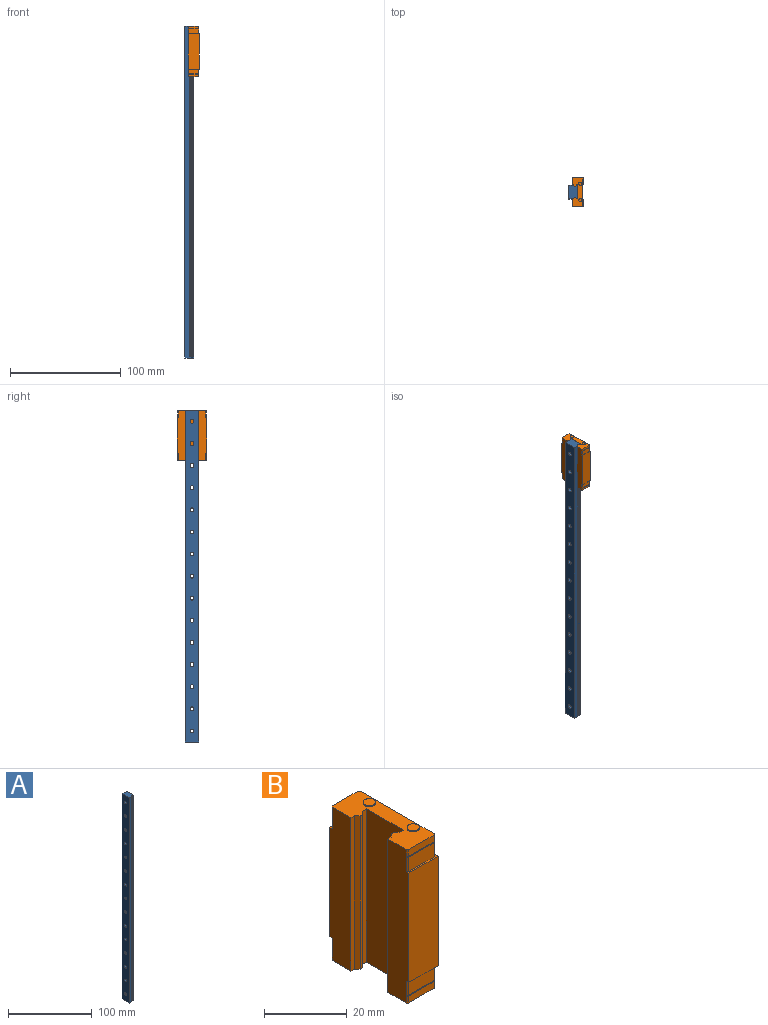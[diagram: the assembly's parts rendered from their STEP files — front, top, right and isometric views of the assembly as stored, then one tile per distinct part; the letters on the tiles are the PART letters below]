
ASSEMBLY  parts=2 mates=1
PART A: 59 faces, bbox 8x12x300 mm
  f0: plane 300x12mm, normal (1,0,0), area 3175.9mm2, adj f10,f11,f13,f15,f18,f21,f24,f27
  f1: cylinder r=1.75mm len=5.5mm, axis (-1,0,0), area 60.5mm2, adj f5,f14
  f2: plane 300x1mm, normal (0,1,0), area 300mm2, adj f3,f11,f12,f56
  f3: plane 300x1mm, normal (0.71,0.71,0), area 424.3mm2, adj f2,f4,f11,f56
  f4: plane 300x4mm, normal (0,1,0), area 1200mm2, adj f3,f5,f11,f56
  f5: plane 300x12mm, normal (-1,0,0), area 3455.7mm2, adj f1,f4,f6,f11,f16,f19,f22,f25
  f6: plane 300x4mm, normal (0,-1,0), area 1200mm2, adj f5,f7,f11,f56
  f7: plane 300x1mm, normal (0.71,-0.71,0), area 424.3mm2, adj f6,f8,f11,f56
  f8: plane 300x1mm, normal (0,-1,0), area 300mm2, adj f7,f9,f11,f56
  f9: plane 300x1mm, normal (-0.71,-0.71,0), area 424.3mm2, adj f8,f10,f11,f56
  f10: plane 300x1mm, normal (0,-1,0), area 300mm2, adj f0,f9,f11,f56
  f11: plane 12x8mm, normal (0,0,-1), area 92mm2, adj f0,f2,f3,f4,f5,f6,f7,f8
  f12: plane 300x1mm, normal (-0.71,0.71,0), area 424.3mm2, adj f2,f11,f13,f56
  f13: plane 300x1mm, normal (0,1,0), area 300mm2, adj f0,f11,f12,f56
  f14: plane 6x6mm, normal (1,0,0), area 18.7mm2, adj f1,f15
  f15: cylinder r=3mm len=6mm, axis (-1,0,0), area 47.1mm2, adj f0,f14
  f16: cylinder r=1.75mm len=5.5mm, axis (-1,0,0), area 60.5mm2, adj f5,f17
  f17: plane 6x6mm, normal (1,0,0), area 18.7mm2, adj f16,f18
  f18: cylinder r=3mm len=6mm, axis (-1,0,0), area 47.1mm2, adj f0,f17
  f19: cylinder r=1.75mm len=5.5mm, axis (-1,0,0), area 60.5mm2, adj f5,f20
  f20: plane 6x6mm, normal (1,0,0), area 18.7mm2, adj f19,f21
  f21: cylinder r=3mm len=6mm, axis (-1,0,0), area 47.1mm2, adj f0,f20
  f22: cylinder r=1.75mm len=5.5mm, axis (-1,0,0), area 60.5mm2, adj f5,f23
  f23: plane 6x6mm, normal (1,0,0), area 18.7mm2, adj f22,f24
  f24: cylinder r=3mm len=6mm, axis (-1,0,0), area 47.1mm2, adj f0,f23
  f25: cylinder r=1.75mm len=5.5mm, axis (-1,0,0), area 60.5mm2, adj f5,f26
  f26: plane 6x6mm, normal (1,0,0), area 18.7mm2, adj f25,f27
  f27: cylinder r=3mm len=6mm, axis (-1,0,0), area 47.1mm2, adj f0,f26
  f28: cylinder r=1.75mm len=5.5mm, axis (-1,0,0), area 60.5mm2, adj f5,f29
  f29: plane 6x6mm, normal (1,0,0), area 18.7mm2, adj f28,f30
  f30: cylinder r=3mm len=6mm, axis (-1,0,0), area 47.1mm2, adj f0,f29
  f31: cylinder r=1.75mm len=5.5mm, axis (-1,0,0), area 60.5mm2, adj f5,f32
  f32: plane 6x6mm, normal (1,0,0), area 18.7mm2, adj f31,f33
  f33: cylinder r=3mm len=6mm, axis (-1,0,0), area 47.1mm2, adj f0,f32
  f34: cylinder r=1.75mm len=5.5mm, axis (-1,0,0), area 60.5mm2, adj f5,f35
  f35: plane 6x6mm, normal (1,0,0), area 18.7mm2, adj f34,f36
  f36: cylinder r=3mm len=6mm, axis (-1,0,0), area 47.1mm2, adj f0,f35
  f37: cylinder r=1.75mm len=5.5mm, axis (-1,0,0), area 60.5mm2, adj f5,f38
  f38: plane 6x6mm, normal (1,0,0), area 18.7mm2, adj f37,f39
  f39: cylinder r=3mm len=6mm, axis (-1,0,0), area 47.1mm2, adj f0,f38
  f40: cylinder r=1.75mm len=5.5mm, axis (-1,0,0), area 60.5mm2, adj f5,f41
  f41: plane 6x6mm, normal (1,0,0), area 18.7mm2, adj f40,f42
  f42: cylinder r=3mm len=6mm, axis (-1,0,0), area 47.1mm2, adj f0,f41
  f43: cylinder r=1.75mm len=5.5mm, axis (-1,0,0), area 60.5mm2, adj f5,f44
  f44: plane 6x6mm, normal (1,0,0), area 18.7mm2, adj f43,f45
  f45: cylinder r=3mm len=6mm, axis (-1,0,0), area 47.1mm2, adj f0,f44
  f46: cylinder r=1.75mm len=5.5mm, axis (-1,0,0), area 60.5mm2, adj f5,f47
  f47: plane 6x6mm, normal (1,0,0), area 18.7mm2, adj f46,f48
  f48: cylinder r=3mm len=6mm, axis (-1,0,0), area 47.1mm2, adj f0,f47
  f49: cylinder r=1.75mm len=5.5mm, axis (-1,0,0), area 60.5mm2, adj f5,f50
  f50: plane 6x6mm, normal (1,0,0), area 18.7mm2, adj f49,f51
  f51: cylinder r=3mm len=6mm, axis (-1,0,0), area 47.1mm2, adj f0,f50
  f52: cylinder r=1.75mm len=5.5mm, axis (-1,0,0), area 60.5mm2, adj f5,f53
  f53: plane 6x6mm, normal (1,0,0), area 18.7mm2, adj f52,f54
  f54: cylinder r=3mm len=6mm, axis (-1,0,0), area 47.1mm2, adj f0,f53
  f55: cylinder r=1.75mm len=5.5mm, axis (-1,0,0), area 60.5mm2, adj f5,f57
  f56: plane 12x8mm, normal (0,0,1), area 92mm2, adj f0,f2,f3,f4,f5,f6,f7,f8
  f57: plane 6x6mm, normal (1,0,0), area 18.7mm2, adj f55,f58
  f58: cylinder r=3mm len=6mm, axis (-1,0,0), area 47.1mm2, adj f0,f57
PART B: 82 faces, bbox 10x27x46 mm
  f0: plane 25.29x3.9mm, normal (1,0,0), area 98.6mm2, adj f19,f48,f53,f61
  f1: plane 32.4x13mm, normal (1,0,0), area 421.2mm2, adj f21,f24,f25,f38
  f2: plane 25.29x3.9mm, normal (1,0,0), area 98.6mm2, adj f12,f13,f58,f63
  f3: plane 25.29x2mm, normal (1,0,0), area 50.6mm2, adj f11,f14,f42,f56
  f4: plane 25.29x2mm, normal (1,0,0), area 50.6mm2, adj f18,f45,f49,f55
  f5: plane 8.79x4.2mm, normal (0,1,0), area 36.9mm2, adj f10,f12,f38,f58
  f6: plane 8.79x4.2mm, normal (0,-1,0), area 36.9mm2, adj f13,f15,f38,f58
  f7: plane 8.79x2mm, normal (0,-1,0), area 17.6mm2, adj f17,f18,f45,f55
  f8: plane 8.79x2mm, normal (0,1,0), area 17.6mm2, adj f45,f49,f51,f55
  f9: plane 2x0.35mm, normal (-0.71,0.71,0), area 1mm2, adj f28,f42,f43,f56
  f10: plane 4.2x0.35mm, normal (-0.71,0.71,0), area 2.1mm2, adj f5,f28,f38,f58
  f11: plane 2x0.35mm, normal (0.71,0.71,0), area 1mm2, adj f3,f42,f43,f56
  f12: plane 4.2x0.35mm, normal (0.71,0.71,0), area 2mm2, adj f2,f5,f38,f58,f63,f64
  f13: plane 4.2x0.35mm, normal (0.71,-0.71,0), area 2mm2, adj f2,f6,f38,f58,f63,f64
  f14: plane 2x0.35mm, normal (0.71,-0.71,0), area 1mm2, adj f3,f42,f44,f56
  f15: plane 4.2x0.35mm, normal (-0.71,-0.71,0), area 2.1mm2, adj f6,f38,f40,f58
  f16: plane 2x0.35mm, normal (-0.71,-0.71,0), area 1mm2, adj f40,f42,f44,f56
  f17: plane 2x0.35mm, normal (-0.71,-0.71,0), area 1mm2, adj f7,f40,f45,f55
  f18: plane 2x0.35mm, normal (0.71,-0.71,0), area 1mm2, adj f4,f7,f45,f55
  f19: plane 4.2x0.35mm, normal (0.71,0.71,0), area 2mm2, adj f0,f21,f50,f53,f60,f61
  f20: plane 4.2x0.35mm, normal (-0.71,0.71,0), area 2.1mm2, adj f21,f28,f50,f53
  f21: plane 27x10mm, normal (0,0,1), area 24.4mm2, adj f1,f19,f20,f22,f23,f24,f25,f26
  f22: plane 32.4x10mm, normal (0,-1,0), area 324mm2, adj f21,f23,f38,f40
  f23: plane 32.4x7mm, normal (1,0,0), area 212.7mm2, adj f21,f22,f24,f38,f79,f81
  f24: plane 32.4x0.5mm, normal (0,1,0), area 16.2mm2, adj f1,f21,f23,f38
  f25: plane 32.4x0.5mm, normal (0,-1,0), area 16.2mm2, adj f1,f21,f26,f38
  f26: plane 32.4x7mm, normal (1,0,0), area 212.7mm2, adj f21,f25,f27,f38,f75,f77
  f27: plane 32.4x10mm, normal (0,1,0), area 324mm2, adj f21,f26,f28,f38
  f28: plane 45.4x7.2mm, normal (-1,0,0), area 315.8mm2, adj f9,f10,f20,f21,f27,f29,f38,f42
  f29: plane 45.4x1.12mm, normal (0,-1,0), area 51mm2, adj f28,f30,f42,f45
  f30: plane 45.4x1mm, normal (-0.71,-0.71,0), area 64.2mm2, adj f29,f31,f42,f45
  f31: plane 45.4x0.75mm, normal (0,-1,0), area 34.1mm2, adj f30,f32,f42,f45
  f32: plane 45.4x1mm, normal (0.71,-0.71,0), area 64.2mm2, adj f31,f33,f42,f45
  f33: plane 45.4x1.42mm, normal (0,-1,0), area 64.7mm2, adj f32,f34,f42,f45
  f34: plane 45.4x12.6mm, normal (-1,0,0), area 572mm2, adj f33,f35,f42,f45
  f35: plane 45.4x1.42mm, normal (0,1,0), area 64.7mm2, adj f34,f36,f42,f45
  f36: plane 45.4x1mm, normal (0.71,0.71,0), area 64.2mm2, adj f35,f37,f42,f45
  f37: plane 45.4x0.75mm, normal (0,1,0), area 34.1mm2, adj f36,f39,f42,f45
  f38: plane 27x10mm, normal (0,0,-1), area 24.4mm2, adj f1,f5,f6,f10,f12,f13,f15,f22
  f39: plane 45.4x1mm, normal (-0.71,0.71,0), area 64.2mm2, adj f37,f41,f42,f45
  f40: plane 45.4x7.2mm, normal (-1,0,0), area 315.8mm2, adj f15,f16,f17,f21,f22,f38,f41,f42
  f41: plane 45.4x1.12mm, normal (0,1,0), area 51mm2, adj f39,f40,f42,f45
  f42: plane 26x9.5mm, normal (0,0,-1), area 169.3mm2, adj f3,f9,f11,f14,f16,f28,f29,f30
  f43: plane 8.79x2mm, normal (0,1,0), area 17.6mm2, adj f9,f11,f42,f56
  f44: plane 8.79x2mm, normal (0,-1,0), area 17.6mm2, adj f14,f16,f42,f56
  f45: plane 26x9.5mm, normal (0,0,1), area 169.3mm2, adj f4,f7,f8,f17,f18,f28,f29,f30
  f46: plane 4.2x0.35mm, normal (-0.71,-0.71,0), area 2.1mm2, adj f21,f40,f47,f53
  f47: plane 8.79x4.2mm, normal (0,-1,0), area 36.9mm2, adj f21,f46,f48,f53
  f48: plane 4.2x0.35mm, normal (0.71,-0.71,0), area 2mm2, adj f0,f21,f47,f53,f60,f61
  f49: plane 2x0.35mm, normal (0.71,0.71,0), area 1mm2, adj f4,f8,f45,f55
  f50: plane 8.79x4.2mm, normal (0,1,0), area 36.9mm2, adj f19,f20,f21,f53
  f51: plane 2x0.35mm, normal (-0.71,0.71,0), area 1mm2, adj f8,f28,f45,f55
  f52: plane 9.2x0.3mm, normal (0,1,0), area 2.8mm2, adj f28,f53,f55,f65
  f53: plane 26x9.5mm, normal (0,0,1), area 14.1mm2, adj f0,f19,f20,f46,f47,f48,f50,f52
  f54: plane 9.2x0.3mm, normal (0,-1,0), area 2.8mm2, adj f40,f53,f55,f65
  f55: plane 26x9.5mm, normal (0,0,-1), area 14.1mm2, adj f4,f7,f8,f17,f18,f49,f51,f52
  f56: plane 26x9.5mm, normal (0,0,1), area 14.1mm2, adj f3,f9,f11,f14,f16,f43,f44,f57
  f57: plane 9.2x0.3mm, normal (0,-1,0), area 2.8mm2, adj f40,f56,f58,f62
  f58: plane 26x9.5mm, normal (0,0,-1), area 14.1mm2, adj f2,f5,f6,f10,f12,f13,f15,f57
  f59: plane 9.2x0.3mm, normal (0,1,0), area 2.8mm2, adj f28,f56,f58,f62
  f60: plane 25.89x0.3mm, normal (1,0,0), area 7.8mm2, adj f19,f21,f48,f61
  f61: plane 25.89x0.3mm, normal (0,0,-1), area 7.7mm2, adj f0,f19,f48,f60
  f62: plane 25.29x0.3mm, normal (1,0,0), area 7.6mm2, adj f56,f57,f58,f59
  f63: plane 25.89x0.3mm, normal (0,0,1), area 7.7mm2, adj f2,f12,f13,f64
  f64: plane 25.89x0.3mm, normal (1,0,0), area 7.8mm2, adj f12,f13,f38,f63
  f65: plane 25.29x0.3mm, normal (1,0,0), area 7.6mm2, adj f52,f53,f54,f55
  f66: plane 3x3mm, normal (0,0,1), area 7.1mm2, adj f67
  f67: cylinder r=1.5mm len=3mm, axis (0,0,-1), area 2.8mm2, adj f45,f66
  f68: cylinder r=1.5mm len=3mm, axis (0,0,-1), area 2.8mm2, adj f42,f69
  f69: plane 3x3mm, normal (0,0,-1), area 7.1mm2, adj f68
  f70: plane 3x3mm, normal (0,0,1), area 7.1mm2, adj f71
  f71: cylinder r=1.5mm len=3mm, axis (0,0,-1), area 2.8mm2, adj f45,f70
  f72: cylinder r=1.5mm len=3mm, axis (0,0,-1), area 2.8mm2, adj f42,f73
  f73: plane 3x3mm, normal (0,0,-1), area 7.1mm2, adj f72
  f74: plane 3x3mm, normal (1,0,0), area 7.1mm2, adj f75
  f75: cylinder r=1.5mm len=3.5mm, axis (-1,0,0), area 33mm2, adj f26,f74
  f76: plane 3x3mm, normal (1,0,0), area 7.1mm2, adj f77
  f77: cylinder r=1.5mm len=3.5mm, axis (-1,0,0), area 33mm2, adj f26,f76
  f78: plane 3x3mm, normal (1,0,0), area 7.1mm2, adj f79
  f79: cylinder r=1.5mm len=3.5mm, axis (-1,0,0), area 33mm2, adj f23,f78
  f80: plane 3x3mm, normal (1,0,0), area 7.1mm2, adj f81
  f81: cylinder r=1.5mm len=3.5mm, axis (-1,0,0), area 33mm2, adj f23,f80
PLACE A at identity fixed
PLACE B t=(0,22,277.3)mm
MATE slider B.f42 <-> A.f11  axis (0,0,-1) through (8.3,0,254.6)mm
